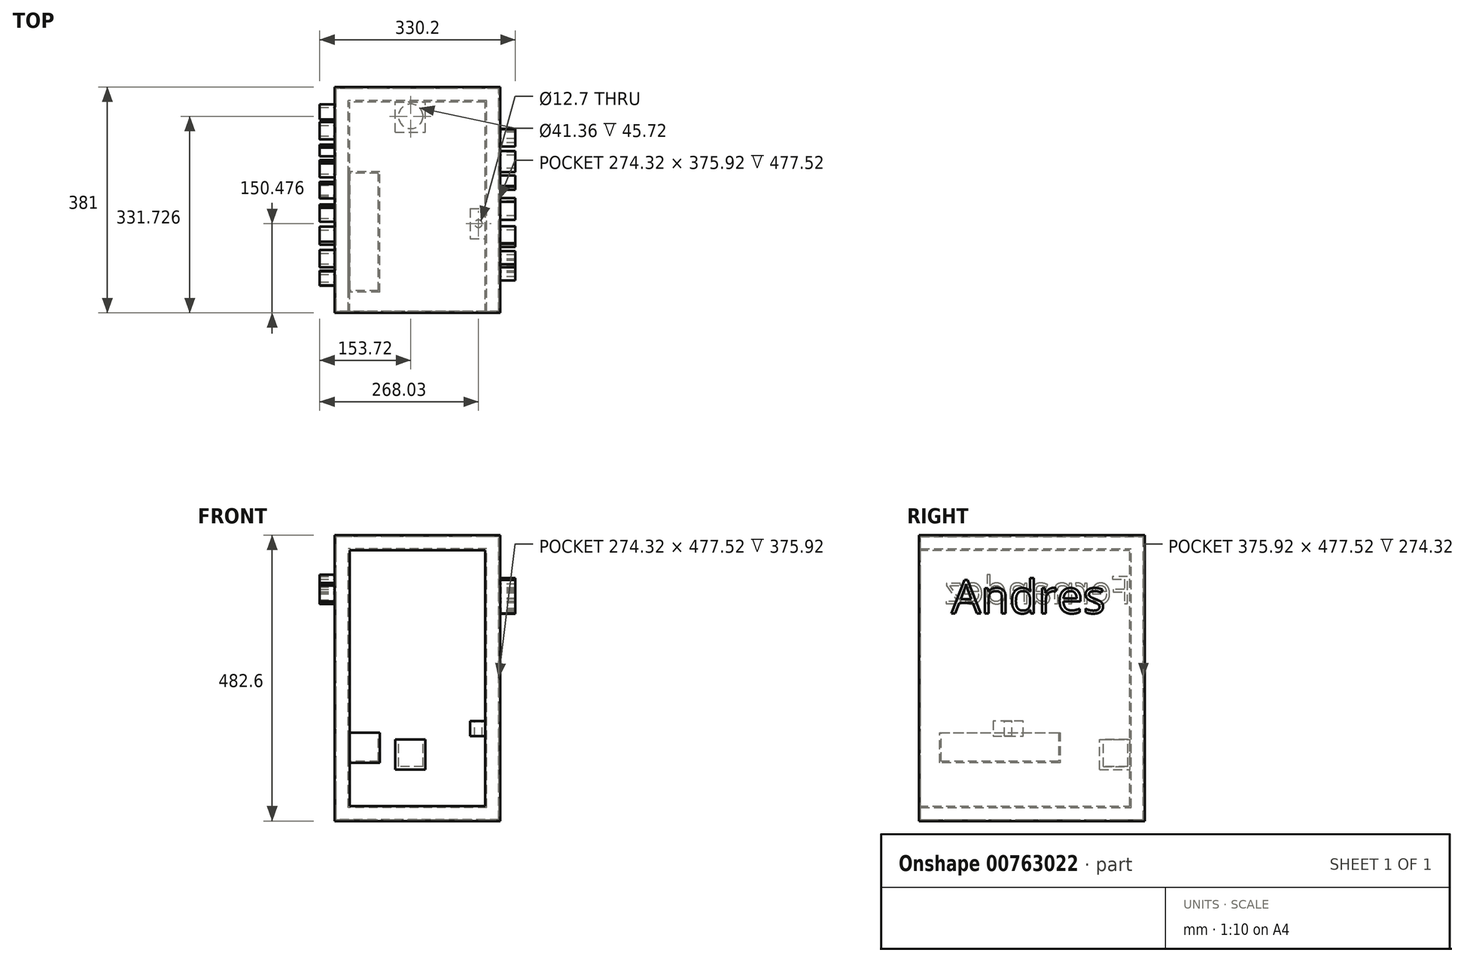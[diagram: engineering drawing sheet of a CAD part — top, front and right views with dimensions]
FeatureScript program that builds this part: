
annotation { "Feature Type Name" : "Feature", "Feature Type Description" : "" }
export const myFeature = defineFeature(function(context is Context, id is Id, definition is map)
    precondition{}
    {
        {
            var Q0;
            Q0=qCreatedBy(makeId("Front.planeOp"),FACE);
            var sketch = newSketch(context, id + "F0", { "sketchPlane" : qUnion([Q0])});
            skLineSegment(sketch, "E0", {"start": v(0, 0) * mm, "end": v(139.7, 0) * mm});
            skLineSegment(sketch, "E1", {"start": v(0, 0) * mm, "end": v(-139.7, 0) * mm});
            skLineSegment(sketch, "E2", {"start": v(-139.7, 0) * mm, "end": v(-139.7, 482.6) * mm});
            skLineSegment(sketch, "E3", {"start": v(139.7, 0) * mm, "end": v(139.7, 482.6) * mm});
            skLineSegment(sketch, "E4", {"start": v(139.7, 482.6) * mm, "end": v(-139.7, 482.6) * mm});
            skSolve(sketch);
        }
        {
            var Q0;
            Q0=makeQuery(id+"F0.imprint","IMPRINT",FACE,{"disambiguationData":[TD([[makeQuery(id+"F0.imprint","IMPRINT",EDGE,{"derivedFrom":sQuery(id+"F0.wireOp",EDGE,"E0")}),1.0]])]});
            extrude(context, id + "F1", {"entities" : qUnion([Q0]), "depth" : 381 * mm, "offsetDistance" : 25.4 * mm});
        }
        {
            var Q0;
            Q0=makeQuery(id+"F1.opExtrude","CAP_FACE",FACE,{"disambiguationData":[OSD([sQuery(id+"F0.wireOp",EDGE,"E0"),sQuery(id+"F0.wireOp",EDGE,"E1"),sQuery(id+"F0.wireOp",EDGE,"E2"),sQuery(id+"F0.wireOp",EDGE,"E3"),sQuery(id+"F0.wireOp",EDGE,"E4")])],"isStart":false});
            shell(context, id + "F2", {"entities" : qUnion([Q0]), "thickness" : 25.4 * mm});
        }
        {
            var Q0;
            Q0=makeQuery(id+"F2.opShell","OFFSET_FACE",FACE,{"disambiguationData":[OSD([sQuery(id+"F0.wireOp",EDGE,"E2")])]});
            var sketch = newSketch(context, id + "F3", { "sketchPlane" : qUnion([Q0])});
            skLineSegment(sketch, "E5", {"start": v(-346.16, 149.1) * mm, "end": v(-142.96, 149.1) * mm});
            skLineSegment(sketch, "E6", {"start": v(-142.96, 149.1) * mm, "end": v(-142.96, 98.3) * mm});
            skLineSegment(sketch, "E7", {"start": v(-142.96, 98.3) * mm, "end": v(-346.16, 98.3) * mm});
            skLineSegment(sketch, "E8", {"start": v(-346.16, 98.3) * mm, "end": v(-346.16, 149.1) * mm});
            skSolve(sketch);
        }
        {
            var Q0;
            Q0=makeQuery(id+"F3.imprint","IMPRINT",FACE,{"disambiguationData":[TD([[makeQuery(id+"F3.imprint","IMPRINT",EDGE,{"derivedFrom":sQuery(id+"F3.wireOp",EDGE,"E5")}),-1.0]])]});
            extrude(context, id + "F4", {"entities" : qUnion([Q0]), "operationType" : NewBodyOperationType.ADD, "depth" : 50.8 * mm, "offsetDistance" : 25.4 * mm});
        }
        {
            var Q0;
            Q0=makeQuery(id+"F4.opExtrude","SWEPT_FACE",FACE,{"disambiguationData":[OSD([sQuery(id+"F3.wireOp",EDGE,"E5")])]});
            shell(context, id + "F5", {"entities" : qUnion([Q0]), "thickness" : 2.54 * mm});
        }
        {
            var Q0;
            Q0=makeQuery(id+"F2.opShell","OFFSET_FACE",FACE,{"disambiguationData":[OSD([sQuery(id+"F0.wireOp",EDGE,"E3")])]});
            var sketch = newSketch(context, id + "F6", { "sketchPlane" : qUnion([Q0])});
            skLineSegment(sketch, "E9", {"start": v(205.12, 168.35) * mm, "end": v(255.92, 168.35) * mm});
            skLineSegment(sketch, "E10", {"start": v(255.92, 168.35) * mm, "end": v(255.92, 142.95) * mm});
            skLineSegment(sketch, "E11", {"start": v(255.92, 142.95) * mm, "end": v(205.12, 142.95) * mm});
            skLineSegment(sketch, "E12", {"start": v(205.12, 142.95) * mm, "end": v(205.12, 168.35) * mm});
            skSolve(sketch);
        }
        {
            var Q0;
            Q0=makeQuery(id+"F6.imprint","IMPRINT",FACE,{"disambiguationData":[TD([[makeQuery(id+"F6.imprint","IMPRINT",EDGE,{"derivedFrom":sQuery(id+"F6.wireOp",EDGE,"E9")}),-1.0]])]});
            extrude(context, id + "F7", {"entities" : qUnion([Q0]), "operationType" : NewBodyOperationType.ADD, "depth" : 25.4 * mm, "offsetDistance" : 25.4 * mm});
        }
        {
            var Q0;
            Q0=makeQuery(id+"F7.opExtrude","SWEPT_FACE",FACE,{"disambiguationData":[OSD([sQuery(id+"F6.wireOp",EDGE,"E9")])]});
            var sketch = newSketch(context, id + "F8", { "sketchPlane" : qUnion([Q0])});
            skCircle(sketch, "E13", {"center": v(102.93, -230.52) * mm, "radius": 6.35 * mm});
            skPoint(sketch, "E13.centerSnap0", {"position": v(114.3, -230.52) * mm});
            skSolve(sketch);
        }
        {
            var Q0;
            Q0=makeQuery(id+"F8.imprint","IMPRINT",FACE,{"disambiguationData":[TD([[makeQuery(id+"F8.imprint","IMPRINT",EDGE,{"derivedFrom":sQuery(id+"F8.wireOp",EDGE,"E13")}),1.0]])]});
            extrude(context, id + "F9", {"entities" : qUnion([Q0]), "operationType" : NewBodyOperationType.REMOVE, "depth" : -25.4 * mm, "offsetDistance" : 25.4 * mm});
        }
        {
            var Q0;
            Q0=makeQuery(id+"F1.opExtrude","SWEPT_FACE",FACE,{"disambiguationData":[OSD([sQuery(id+"F0.wireOp",EDGE,"E3")])]});
            var sketch = newSketch(context, id + "F10", { "sketchPlane" : qUnion([Q0])});
            skText(sketch, "E14", { "text": "Andres", "fontName": "OpenSans-Regular.ttf"});
            const initialGuessF10  = {"E14": [-0.32645, 0.35052, 1, 0, 0.0566]};
            skSetInitialGuess(sketch, initialGuessF10);
            skSolve(sketch);
        }
        {
            var Q0;
            Q0 = qSketchRegion(id + "F10", true);
            extrude(context, id + "F11", {"entities" : qUnion([Q0]), "operationType" : NewBodyOperationType.ADD, "depth" : 25.4 * mm, "offsetDistance" : 25.4 * mm});
        }
        {
            var Q0;
            Q0=makeQuery(id+"F1.opExtrude","SWEPT_FACE",FACE,{"disambiguationData":[OSD([sQuery(id+"F0.wireOp",EDGE,"E2")])]});
            var sketch = newSketch(context, id + "F12", { "sketchPlane" : qUnion([Q0])});
            skText(sketch, "E15", { "text": "Fernandez", "fontName": "OpenSans-Regular.ttf"});
            const initialGuessF12  = {"E15": [0.02264, 0.36681, 1, 0, 0.04616]};
            skSetInitialGuess(sketch, initialGuessF12);
            skSolve(sketch);
        }
        {
            var Q0;
            Q0 = qSketchRegion(id + "F12", true);
            extrude(context, id + "F13", {"entities" : qUnion([Q0]), "operationType" : NewBodyOperationType.ADD, "depth" : 25.4 * mm, "offsetDistance" : 25.4 * mm});
        }
        {
            var Q0;
            Q0=makeQuery(id+"F2.opShell","OFFSET_FACE",FACE,{"disambiguationData":[OSD([sQuery(id+"F0.wireOp",EDGE,"E0"),sQuery(id+"F0.wireOp",EDGE,"E1"),sQuery(id+"F0.wireOp",EDGE,"E2"),sQuery(id+"F0.wireOp",EDGE,"E3"),sQuery(id+"F0.wireOp",EDGE,"E4")])]});
            var sketch = newSketch(context, id + "F14", { "sketchPlane" : qUnion([Q0])});
            skLineSegment(sketch, "E16", {"start": v(-37.37, 137.57) * mm, "end": v(13.43, 137.57) * mm});
            skLineSegment(sketch, "E17", {"start": v(13.43, 137.57) * mm, "end": v(13.43, 86.77) * mm});
            skLineSegment(sketch, "E18", {"start": v(13.43, 86.77) * mm, "end": v(-37.37, 86.77) * mm});
            skLineSegment(sketch, "E19", {"start": v(-37.37, 86.77) * mm, "end": v(-37.37, 137.57) * mm});
            skSolve(sketch);
        }
        {
            var Q0;
            Q0=makeQuery(id+"F14.imprint","IMPRINT",FACE,{"disambiguationData":[TD([[makeQuery(id+"F14.imprint","IMPRINT",EDGE,{"derivedFrom":sQuery(id+"F14.wireOp",EDGE,"E16")}),-1.0]])]});
            extrude(context, id + "F15", {"entities" : qUnion([Q0]), "operationType" : NewBodyOperationType.ADD, "depth" : 50.8 * mm, "offsetDistance" : 25.4 * mm});
        }
        {
            var Q0;
            Q0=makeQuery(id+"F15.opExtrude","SWEPT_FACE",FACE,{"disambiguationData":[OSD([sQuery(id+"F14.wireOp",EDGE,"E16")])]});
            var sketch = newSketch(context, id + "F16", { "sketchPlane" : qUnion([Q0])});
            skCircle(sketch, "E20", {"center": v(-11.38, -49.27) * mm, "radius": 20.68 * mm});
            skSolve(sketch);
        }
        {
            var Q0;
            Q0=makeQuery(id+"F16.imprint","IMPRINT",FACE,{"disambiguationData":[TD([[makeQuery(id+"F16.imprint","IMPRINT",EDGE,{"derivedFrom":sQuery(id+"F16.wireOp",EDGE,"E20")}),1.0]])]});
            extrude(context, id + "F17", {"entities" : qUnion([Q0]), "operationType" : NewBodyOperationType.REMOVE, "oppositeDirection" : true, "depth" : 45.72 * mm, "offsetDistance" : 25.4 * mm});
        }
    });
